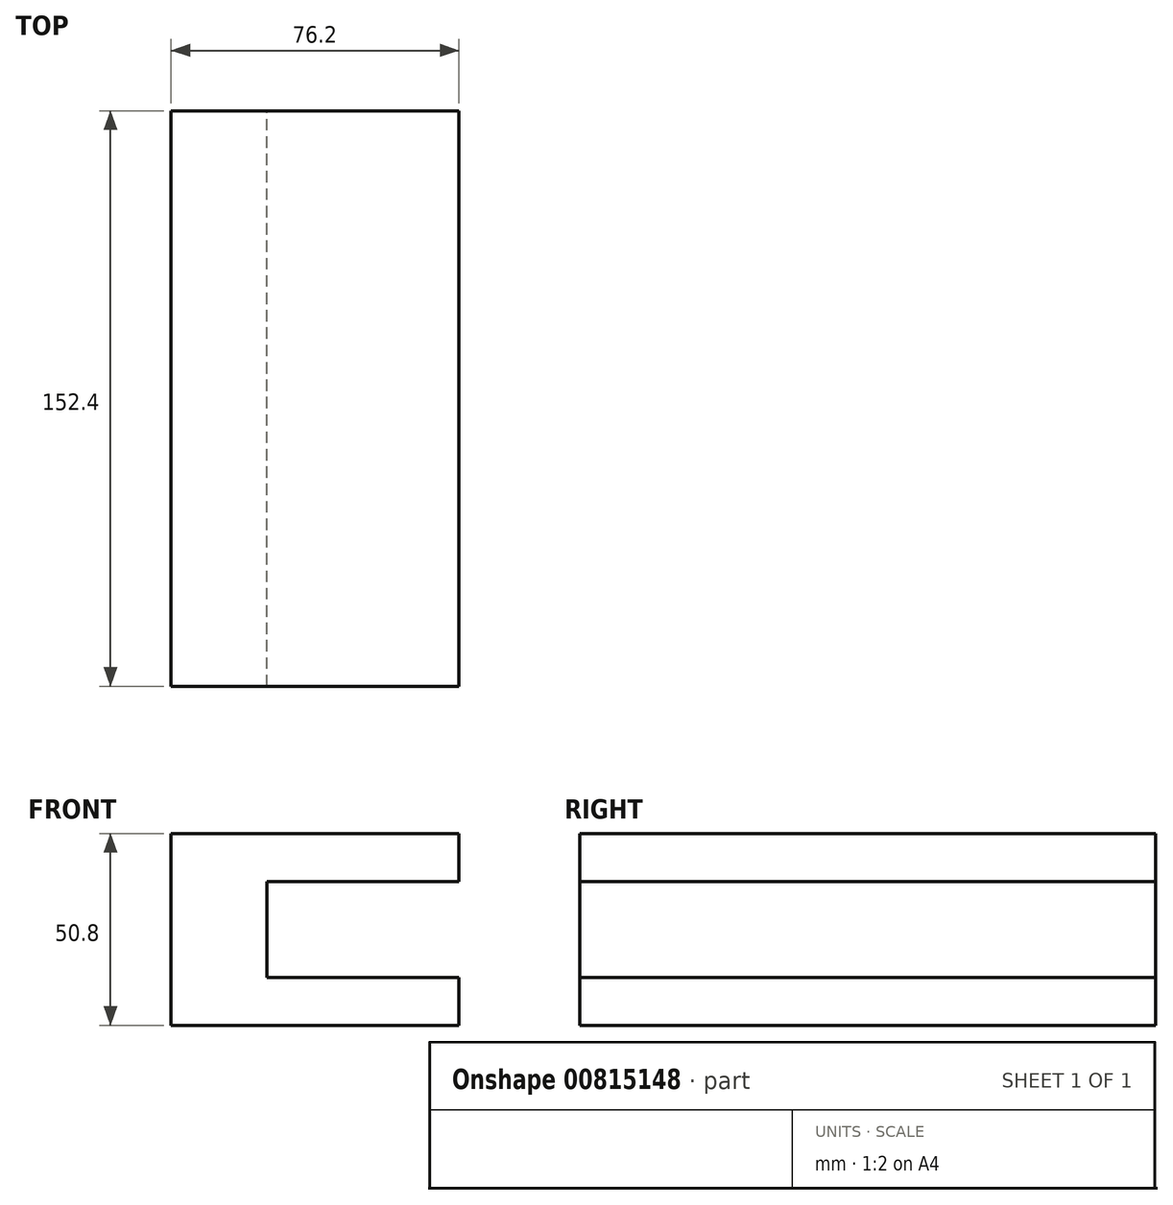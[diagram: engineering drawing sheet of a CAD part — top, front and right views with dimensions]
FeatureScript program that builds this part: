
annotation { "Feature Type Name" : "Feature", "Feature Type Description" : "" }
export const myFeature = defineFeature(function(context is Context, id is Id, definition is map)
    precondition{}
    {
        {
            var Q0;
            Q0=qCreatedBy(makeId("Front.planeOp"),FACE);
            var sketch = newSketch(context, id + "F0", { "sketchPlane" : qUnion([Q0])});
            skLineSegment(sketch, "E0", {"start": v(0, 0) * mm, "end": v(0, 50.8) * mm});
            skLineSegment(sketch, "E1", {"start": v(0, 50.8) * mm, "end": v(76.2, 50.8) * mm});
            skLineSegment(sketch, "E2", {"start": v(76.2, 50.8) * mm, "end": v(76.2, 38.1) * mm});
            skLineSegment(sketch, "E3", {"start": v(76.2, 38.1) * mm, "end": v(25.4, 38.1) * mm});
            skLineSegment(sketch, "E4", {"start": v(25.4, 38.1) * mm, "end": v(25.4, 12.7) * mm});
            skLineSegment(sketch, "E5", {"start": v(25.4, 12.7) * mm, "end": v(76.2, 12.7) * mm});
            skLineSegment(sketch, "E6", {"start": v(76.2, 12.7) * mm, "end": v(76.2, 0) * mm});
            skLineSegment(sketch, "E7", {"start": v(0, 0) * mm, "end": v(76.2, 0) * mm});
            skSolve(sketch);
        }
        {
            var Q0;
            Q0 = qSketchRegion(id + "F0", true);
            extrude(context, id + "F1", {"entities" : qUnion([Q0]), "depth" : 152.4 * mm, "offsetDistance" : 25.4 * mm});
        }
    });
